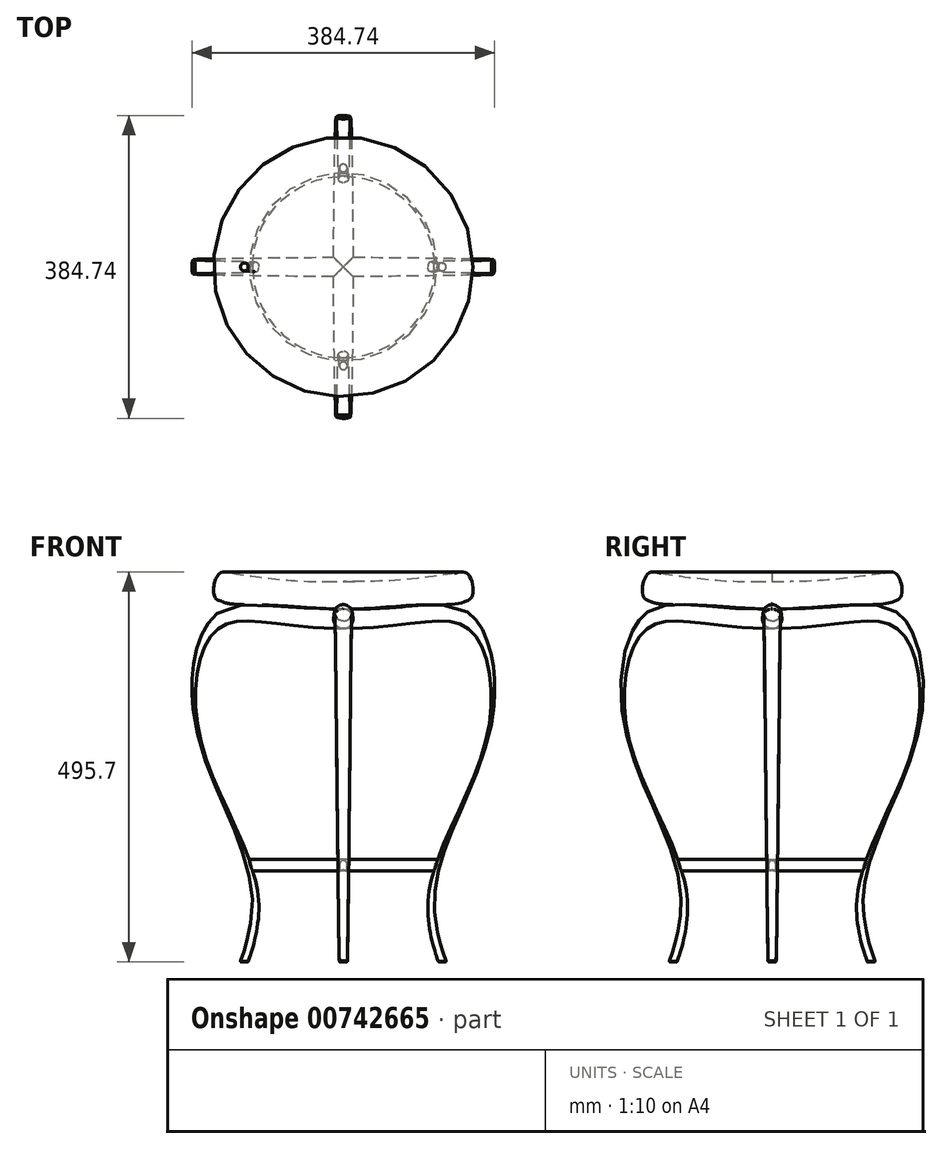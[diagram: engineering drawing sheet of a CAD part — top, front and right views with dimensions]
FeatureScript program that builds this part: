
annotation { "Feature Type Name" : "Feature", "Feature Type Description" : "" }
export const myFeature = defineFeature(function(context is Context, id is Id, definition is map)
    precondition{}
    {
        {
            var Q0;
            Q0=qCreatedBy(makeId("Front.planeOp"),FACE);
            var sketch = newSketch(context, id + "F0", { "sketchPlane" : qUnion([Q0])});
            skFitSpline(sketch, "E0", {"points": [v(0, 0) * mm, v(-158.72, 0) * mm, v(-182.34, -137.41) * mm, v(-107.58, -345.26) * mm, v(-120.92, -423.55) * mm], "startDerivative": vector(-970.97, 0) * mm, "endDerivative": vector(-13.41, -57.5) * mm});
            skLineSegment(sketch, "E1", {"start": v(0, 0) * mm, "end": v(0, -420) * mm, "construction": true});
            skLineSegment(sketch, "E2", {"start": v(0, 0) * mm, "end": v(98.1, 0) * mm, "construction": true});
            skSolve(sketch);
        }
        {
            var Q0;
            Q0=sQuery(id+"F0.wireOp",VERTEX,"E0.end");
            var Q1;
            Q1=qCreatedBy(makeId("Top.planeOp"),FACE);
            cPlane(context, id + "F1", {"entities" : qUnion([Q0, Q1]), "cplaneType" : CPlaneType.PLANE_POINT, "offset" : 25 * mm, "width" : 150 * mm, "height" : 150 * mm});
        }
        {
            var Q0;
            Q0=qCreatedBy(id+"F1.planeOp",FACE);
            var sketch = newSketch(context, id + "F2", { "sketchPlane" : qUnion([Q0])});
            skCircle(sketch, "E3", {"center": v(-125.92, 0) * mm, "radius": 5 * mm});
            skLineSegment(sketch, "E4", {"start": v(-125.92, 0) * mm, "end": v(-120.92, 0) * mm, "construction": true});
            skSolve(sketch);
        }
        {
            var Q0;
            Q0=qCreatedBy(makeId("Right.planeOp"),FACE);
            var sketch = newSketch(context, id + "F3", { "sketchPlane" : qUnion([Q0])});
            skCircle(sketch, "E5", {"center": v(0, 12.5) * mm, "radius": 12.5 * mm});
            skLineSegment(sketch, "E6", {"start": v(0, 12.5) * mm, "end": v(0, 0) * mm, "construction": true});
            skSolve(sketch);
        }
        {
            var Q0;
            Q0=makeQuery(id+"F2.imprint","IMPRINT",FACE,{"disambiguationData":[TD([[makeQuery(id+"F2.imprint","IMPRINT",EDGE,{"derivedFrom":sQuery(id+"F2.wireOp",EDGE,"E3")}),1.0]])]});
            var Q1;
            Q1=makeQuery(id+"F3.imprint","IMPRINT",FACE,{"disambiguationData":[TD([[makeQuery(id+"F3.imprint","IMPRINT",EDGE,{"derivedFrom":sQuery(id+"F3.wireOp",EDGE,"E5")}),1.0]])]});
            var Q2;
            Q2=sQuery(id+"F0.wireOp",EDGE,"E0");
            loft(context, id + "F4", {"addGuides" : true, "sheetProfilesArray" : [{ "sheetProfileEntities" : qUnion([Q0]) }, { "sheetProfileEntities" : qUnion([Q1]) }], "guidesArray" : [{ "guideEntities" : qUnion([Q2]), "guideDerivativeType" : LoftGuideDerivativeType.DEFAULT, "guideDerivativeMagnitude" : 1 }]});
        }
        {
            var Q0;
            Q0=makeQuery(id+"F4.opLoft","MID_CAP_EDGE",EDGE,{"disambiguationData":[OSD([sQuery(id+"F0.wireOp",EDGE,"E0"),sQuery(id+"F2.wireOp",EDGE,"E3")])],"capPos":0.0});
            fillet(context, id + "F5", {"entities" : qUnion([Q0]), "radius" : 1 * mm, "tangentPropagation" : true, "allowEdgeOverflow" : false});
        }
        {
            var Q0;
            Q0=qCreatedBy(makeId("Right.planeOp"),FACE);
            var sketch = newSketch(context, id + "F6", { "sketchPlane" : qUnion([Q0])});
            skLineSegment(sketch, "E7", {"start": v(0, 0) * mm, "end": v(0, -172.28) * mm, "construction": true});
            skSolve(sketch);
        }
        {
            var Q0;
            Q0=makeQuery(id+"F4.opLoft","SWEPT_BODY",BODY,{"disambiguationData":[OSD([sQuery(id+"F0.wireOp",EDGE,"E0"),makeQuery(id+"F2.imprint","IMPRINT",FACE,{"disambiguationData":[TD([[makeQuery(id+"F2.imprint","IMPRINT",EDGE,{"derivedFrom":sQuery(id+"F2.wireOp",EDGE,"E3")}),1.0]])]}),makeQuery(id+"F3.imprint","IMPRINT",FACE,{"disambiguationData":[TD([[makeQuery(id+"F3.imprint","IMPRINT",EDGE,{"derivedFrom":sQuery(id+"F3.wireOp",EDGE,"E5")}),1.0]])]})])]});
            var Q1;
            Q1=sQuery(id+"F6.wireOp",EDGE,"E7");
            circularPattern(context, id + "F7", {"operationType" : NewBodyOperationType.ADD, "entities" : qUnion([Q0]), "axis" : qUnion([Q1]), "angle" : 360 * degree, "instanceCount" : 4, "equalSpace" : true});
        }
        {
            var Q0;
            Q0=qCreatedBy(makeId("Front.planeOp"),FACE);
            var sketch = newSketch(context, id + "F8", { "sketchPlane" : qUnion([Q0])});
            skFitSpline(sketch, "E8", {"points": [v(0, 25) * mm, v(94.74, 29.85) * mm, v(153.35, 34.07) * mm], "startDerivative": vector(218.3, -0.05) * mm, "endDerivative": vector(67.69, 32.2) * mm});
            skFitSpline(sketch, "E9", {"points": [v(141.24, 70.42) * mm, v(67.13, 61.3) * mm, v(0, 60) * mm], "startDerivative": vector(-89.13, -14.79) * mm, "endDerivative": vector(-124.11, 0) * mm});
            skLineSegment(sketch, "E10", {"start": v(0, 60) * mm, "end": v(-25.11, 60) * mm, "construction": true});
            skFitSpline(sketch, "E11", {"points": [v(141.24, 70.42) * mm, v(156.75, 70.42) * mm, v(163.3, 40.18) * mm, v(153.35, 34.07) * mm], "startDerivative": vector(37.09, 6.15) * mm, "endDerivative": vector(-28.69, -13.64) * mm});
            skLineSegment(sketch, "E12", {"start": v(0, 60) * mm, "end": v(0, 25) * mm});
            skSolve(sketch);
        }
        {
            var Q0;
            Q0=makeQuery(id+"F8.imprint","IMPRINT",FACE,{"disambiguationData":[TD([[makeQuery(id+"F8.imprint","IMPRINT",EDGE,{"derivedFrom":sQuery(id+"F8.wireOp",EDGE,"E8")}),1.0]])]});
            var Q1;
            Q1=sQuery(id+"F8.wireOp",EDGE,"E12");
            revolve(context, id + "F9", {"surfaceOperationType" : NewSurfaceOperationType.NEW, "entities" : qUnion([Q0]), "axis" : qUnion([Q1]), "revolveType" : RevolveType.FULL});
        }
        {
            var Q0;
            Q0=qCreatedBy(makeId("Top.planeOp"),FACE);
            cPlane(context, id + "F10", {"entities" : qUnion([Q0]), "cplaneType" : CPlaneType.OFFSET, "offset" : 300 * mm, "oppositeDirection" : true, "width" : 150 * mm, "height" : 150 * mm});
        }
        {
            var Q0;
            Q0=qCreatedBy(id+"F10.planeOp",FACE);
            var sketch = newSketch(context, id + "F11", { "sketchPlane" : qUnion([Q0])});
            skCircle(sketch, "E13", {"center": v(0, 0) * mm, "radius": 116.5 * mm});
            skSolve(sketch);
        }
        {
            var Q0;
            Q0=qCreatedBy(makeId("Right.planeOp"),FACE);
            var sketch = newSketch(context, id + "F12", { "sketchPlane" : qUnion([Q0])});
            skEllipse(sketch, "E14", {"center": v(117.3, -300.21) * mm, "majorRadius": 7.5 * mm, "minorRadius": 0.83 * mm, "majorAxis": v(0.26, 0.97)});
            skLineSegment(sketch, "E15", {"start": v(117.3, -300.21) * mm, "end": v(116.5, -300) * mm, "construction": true});
            skLineSegment(sketch, "E16", {"start": v(117.3, -300.21) * mm, "end": v(117.3, -289.48) * mm, "construction": true});
            skSolve(sketch);
        }
        {
            var Q0;
            Q0=makeQuery(id+"F12.imprint","IMPRINT",FACE,{"disambiguationData":[TD([[makeQuery(id+"F12.imprint","IMPRINT",EDGE,{"derivedFrom":sQuery(id+"F12.wireOp",EDGE,"E14")}),1.0]])]});
            var Q1;
            Q1=sQuery(id+"F11.wireOp",EDGE,"E13");
            sweep(context, id + "F13", {"operationType" : NewBodyOperationType.ADD, "profiles" : qUnion([Q0]), "path" : qUnion([Q1])});
        }
    });
